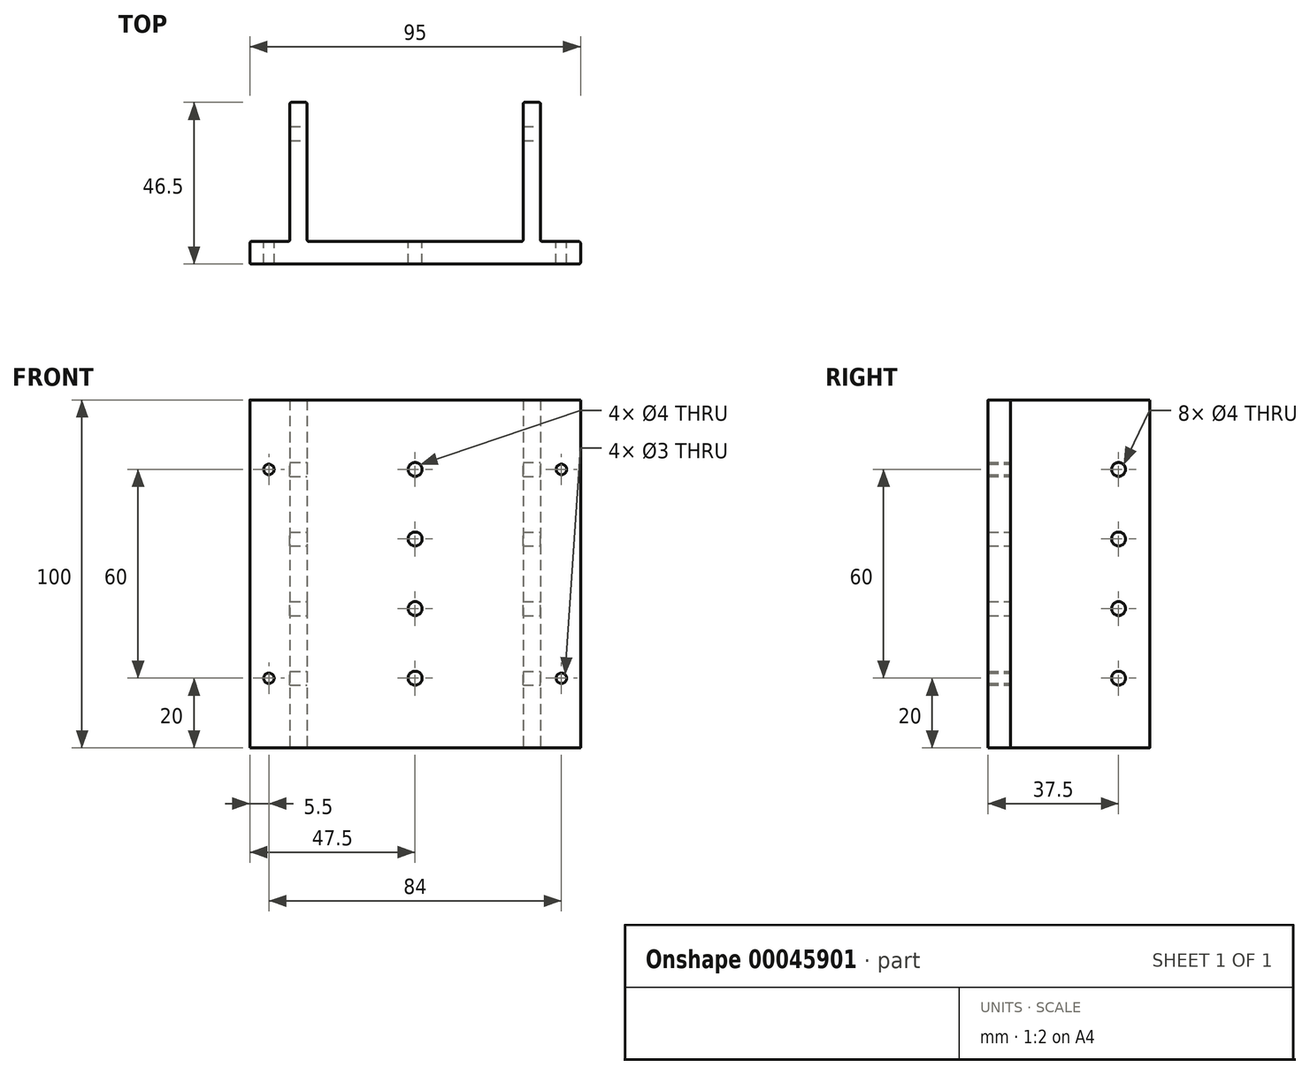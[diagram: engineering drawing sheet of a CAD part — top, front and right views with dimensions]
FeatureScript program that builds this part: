
annotation { "Feature Type Name" : "Feature", "Feature Type Description" : "" }
export const myFeature = defineFeature(function(context is Context, id is Id, definition is map)
    precondition{}
    {
        {
            var Q0;
            Q0=qCreatedBy(makeId("Top.planeOp"),FACE);
            var sketch = newSketch(context, id + "F0", { "sketchPlane" : qUnion([Q0])});
            skLineSegment(sketch, "E0", {"start": v(0.5, 0) * mm, "end": v(94.5, 0) * mm});
            skLineSegment(sketch, "E1", {"start": v(95, 0.5) * mm, "end": v(95, 6) * mm});
            skLineSegment(sketch, "E2", {"start": v(94.5, 6.5) * mm, "end": v(84, 6.5) * mm});
            skLineSegment(sketch, "E3", {"start": v(83.5, 7) * mm, "end": v(83.5, 46) * mm});
            skLineSegment(sketch, "E4", {"start": v(83, 46.5) * mm, "end": v(79, 46.5) * mm});
            skLineSegment(sketch, "E5", {"start": v(78.5, 46) * mm, "end": v(78.5, 7) * mm});
            skLineSegment(sketch, "E6", {"start": v(78, 6.5) * mm, "end": v(17, 6.5) * mm});
            skLineSegment(sketch, "E7", {"start": v(16.5, 7) * mm, "end": v(16.5, 46) * mm});
            skLineSegment(sketch, "E8", {"start": v(16, 46.5) * mm, "end": v(12, 46.5) * mm});
            skLineSegment(sketch, "E9", {"start": v(11.5, 46) * mm, "end": v(11.5, 7) * mm});
            skLineSegment(sketch, "E10", {"start": v(11, 6.5) * mm, "end": v(0.5, 6.5) * mm});
            skLineSegment(sketch, "E11", {"start": v(0, 6) * mm, "end": v(0, 0.5) * mm});
            skPoint(sketch, "E12.visualSharp", {"position": v(11.5, 46.5) * mm});
            skArc(sketch, "E12.filletArc", {"start": v(12, 46.5) * mm, "mid": v(11.65, 46.35) * mm, "end": v(11.5, 46) * mm});
            skPoint(sketch, "E13.visualSharp", {"position": v(16.5, 46.5) * mm});
            skArc(sketch, "E13.filletArc", {"start": v(16.5, 46) * mm, "mid": v(16.35, 46.35) * mm, "end": v(16, 46.5) * mm});
            skPoint(sketch, "E14.visualSharp", {"position": v(16.5, 6.5) * mm});
            skArc(sketch, "E14.filletArc", {"start": v(16.5, 7) * mm, "mid": v(16.65, 6.65) * mm, "end": v(17, 6.5) * mm});
            skPoint(sketch, "E15.visualSharp", {"position": v(11.5, 6.5) * mm});
            skArc(sketch, "E15.filletArc", {"start": v(11, 6.5) * mm, "mid": v(11.35, 6.65) * mm, "end": v(11.5, 7) * mm});
            skPoint(sketch, "E16.visualSharp", {"position": v(0, 6.5) * mm});
            skArc(sketch, "E16.filletArc", {"start": v(0.5, 6.5) * mm, "mid": v(0.15, 6.35) * mm, "end": v(0, 6) * mm});
            skPoint(sketch, "E17.visualSharp", {"position": v(0, 0) * mm});
            skArc(sketch, "E17.filletArc", {"start": v(0, 0.5) * mm, "mid": v(0.15, 0.15) * mm, "end": v(0.5, 0) * mm});
            skPoint(sketch, "E18.visualSharp", {"position": v(95, 0) * mm});
            skArc(sketch, "E18.filletArc", {"start": v(94.5, 0) * mm, "mid": v(94.85, 0.15) * mm, "end": v(95, 0.5) * mm});
            skPoint(sketch, "E19.visualSharp", {"position": v(95, 6.5) * mm});
            skArc(sketch, "E19.filletArc", {"start": v(95, 6) * mm, "mid": v(94.85, 6.35) * mm, "end": v(94.5, 6.5) * mm});
            skPoint(sketch, "E20.visualSharp", {"position": v(83.5, 6.5) * mm});
            skArc(sketch, "E20.filletArc", {"start": v(83.5, 7) * mm, "mid": v(83.65, 6.65) * mm, "end": v(84, 6.5) * mm});
            skPoint(sketch, "E21.visualSharp", {"position": v(78.5, 6.5) * mm});
            skArc(sketch, "E21.filletArc", {"start": v(78, 6.5) * mm, "mid": v(78.35, 6.65) * mm, "end": v(78.5, 7) * mm});
            skPoint(sketch, "E22.visualSharp", {"position": v(83.5, 46.5) * mm});
            skArc(sketch, "E22.filletArc", {"start": v(83.5, 46) * mm, "mid": v(83.35, 46.35) * mm, "end": v(83, 46.5) * mm});
            skPoint(sketch, "E23.visualSharp", {"position": v(78.5, 46.5) * mm});
            skArc(sketch, "E23.filletArc", {"start": v(79, 46.5) * mm, "mid": v(78.65, 46.35) * mm, "end": v(78.5, 46) * mm});
            skSolve(sketch);
        }
        {
            var Q0;
            Q0=makeQuery(id+"F0.imprint","IMPRINT",FACE,{"disambiguationData":[TD([[makeQuery(id+"F0.imprint","IMPRINT",EDGE,{"derivedFrom":sQuery(id+"F0.wireOp",EDGE,"E0")}),1.0]])]});
            extrude(context, id + "F1", {"entities" : qUnion([Q0]), "depth" : 100 * mm});
        }
        {
            var Q0;
            Q0=makeQuery(id+"F1.opExtrude","SWEPT_FACE",FACE,{"disambiguationData":[OSD([sQuery(id+"F0.wireOp",EDGE,"E3")])]});
            var sketch = newSketch(context, id + "F2", { "sketchPlane" : qUnion([Q0])});
            skCircle(sketch, "E24", {"center": v(37.5, 80) * mm, "radius": 2 * mm});
            skCircle(sketch, "E25", {"center": v(37.5, 60) * mm, "radius": 2 * mm});
            skCircle(sketch, "E26", {"center": v(37.5, 40) * mm, "radius": 2 * mm});
            skCircle(sketch, "E27", {"center": v(37.5, 20) * mm, "radius": 2 * mm});
            skSolve(sketch);
        }
        {
            var Q0;
            Q0 = qSketchRegion(id + "F2", true);
            var Q1;
            Q1=makeQuery(id+"F1.opExtrude","SWEPT_FACE",FACE,{"disambiguationData":[OSD([sQuery(id+"F0.wireOp",EDGE,"E9")])]});
            extrude(context, id + "F3", {"entities" : qUnion([Q0]), "operationType" : NewBodyOperationType.REMOVE, "endBound" : BoundingType.UP_TO_SURFACE, "oppositeDirection" : true, "endBoundEntityFace" : qUnion([Q1]), "depth" : 25 * mm});
        }
        {
            var Q0;
            Q0=makeQuery(id+"F1.opExtrude","SWEPT_FACE",FACE,{"disambiguationData":[OSD([sQuery(id+"F0.wireOp",EDGE,"E6")])]});
            var sketch = newSketch(context, id + "F4", { "sketchPlane" : qUnion([Q0])});
            skCircle(sketch, "E28", {"center": v(-47.5, 80) * mm, "radius": 2 * mm});
            skCircle(sketch, "E29", {"center": v(-47.5, 60) * mm, "radius": 2 * mm});
            skCircle(sketch, "E30", {"center": v(-47.5, 40) * mm, "radius": 2 * mm});
            skCircle(sketch, "E31", {"center": v(-47.5, 20) * mm, "radius": 2 * mm});
            skCircle(sketch, "E32", {"center": v(-5.5, 80) * mm, "radius": 1.5 * mm});
            skCircle(sketch, "E33", {"center": v(-5.5, 20) * mm, "radius": 1.5 * mm});
            skCircle(sketch, "E34", {"center": v(-89.5, 80) * mm, "radius": 1.5 * mm});
            skCircle(sketch, "E35", {"center": v(-89.5, 20) * mm, "radius": 1.5 * mm});
            skSolve(sketch);
        }
        {
            var Q0;
            Q0 = qSketchRegion(id + "F4", true);
            extrude(context, id + "F5", {"entities" : qUnion([Q0]), "operationType" : NewBodyOperationType.REMOVE, "endBound" : BoundingType.UP_TO_NEXT, "oppositeDirection" : true, "depth" : 25 * mm});
        }
    });
